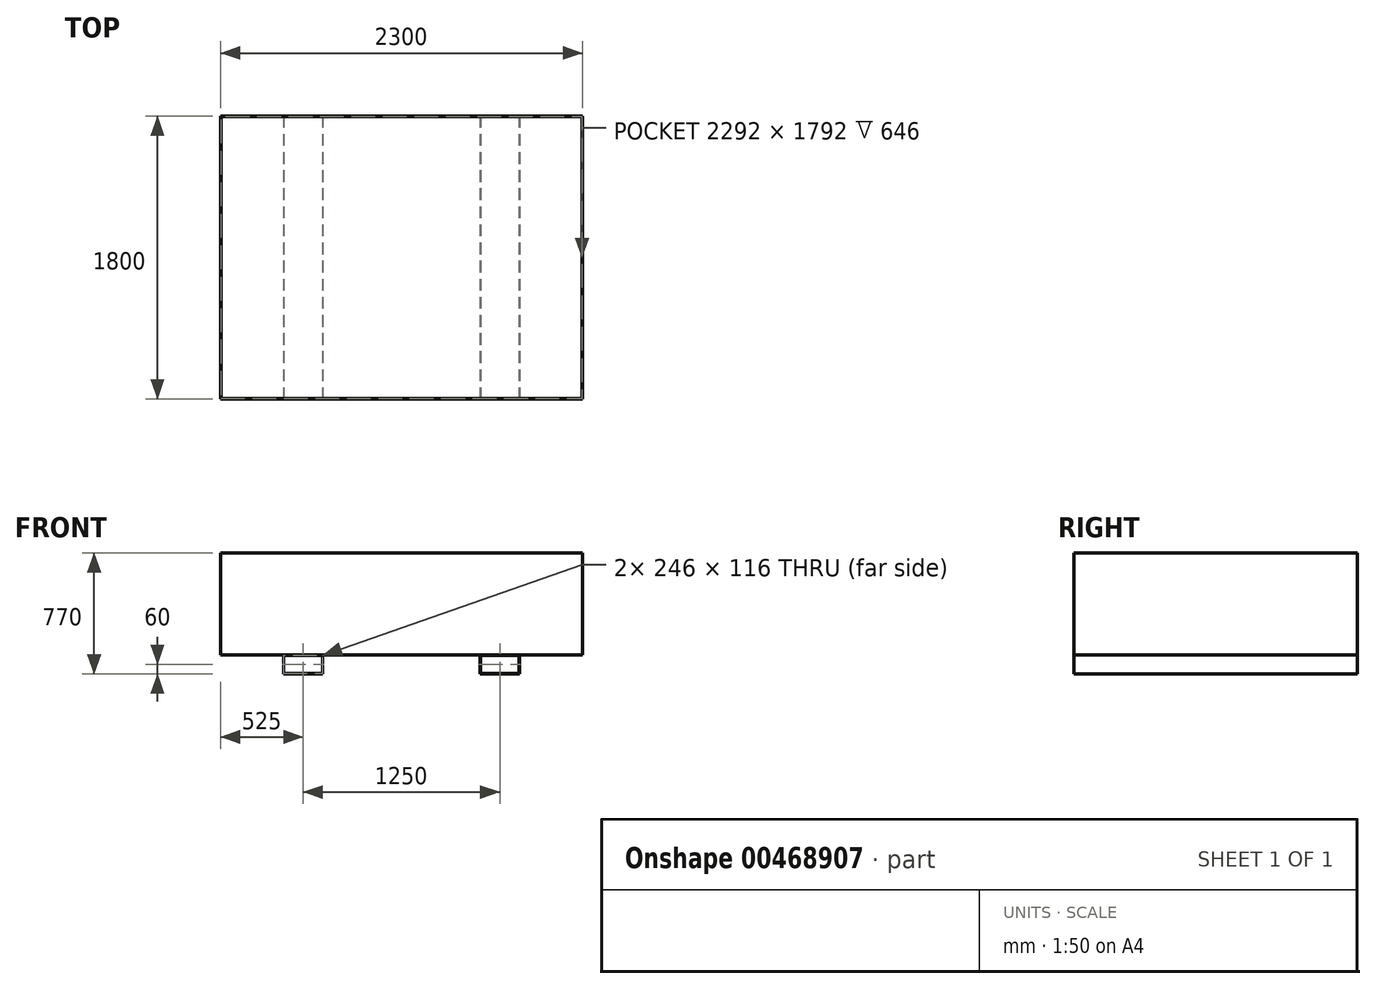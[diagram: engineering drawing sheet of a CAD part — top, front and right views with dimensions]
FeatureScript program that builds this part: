
annotation { "Feature Type Name" : "Feature", "Feature Type Description" : "" }
export const myFeature = defineFeature(function(context is Context, id is Id, definition is map)
    precondition{}
    {
        {
            var Q0;
            Q0=qCreatedBy(makeId("Top.planeOp"),FACE);
            var sketch = newSketch(context, id + "F0", { "sketchPlane" : qUnion([Q0])});
            skLineSegment(sketch, "E0.bottom", {"start": v(-1150, 1775.16) * mm, "end": v(1150, 1775.16) * mm});
            skLineSegment(sketch, "E0.top", {"start": v(-1150, -24.84) * mm, "end": v(1150, -24.84) * mm});
            skLineSegment(sketch, "E0.left", {"start": v(-1150, 1775.16) * mm, "end": v(-1150, -24.84) * mm});
            skLineSegment(sketch, "E0.right", {"start": v(1150, 1775.16) * mm, "end": v(1150, -24.84) * mm});
            skLineSegment(sketch, "E1", {"start": v(0, -153.05) * mm, "end": v(0, 1915.54) * mm, "construction": true});
            skSolve(sketch);
        }
        {
            var Q0;
            Q0=makeQuery(id+"F0.imprint","IMPRINT",FACE,{"disambiguationData":[TD([[makeQuery(id+"F0.imprint","IMPRINT",EDGE,{"derivedFrom":sQuery(id+"F0.wireOp",EDGE,"E0.bottom")}),-1.0]])]});
            extrude(context, id + "F1", {"entities" : qUnion([Q0]), "depth" : 650 * mm});
        }
        {
            var Q0;
            Q0=makeQuery(id+"F1.opExtrude","CAP_FACE",FACE,{"disambiguationData":[OSD([sQuery(id+"F0.wireOp",EDGE,"E0.bottom"),sQuery(id+"F0.wireOp",EDGE,"E0.top"),sQuery(id+"F0.wireOp",EDGE,"E0.left"),sQuery(id+"F0.wireOp",EDGE,"E0.right")])],"isStart":false});
            var Q1;
            Q1=makeQuery(id+"F1.opExtrude","SWEPT_BODY",BODY,{"disambiguationData":[OSD([sQuery(id+"F0.wireOp",EDGE,"E0.bottom"),sQuery(id+"F0.wireOp",EDGE,"E0.top"),sQuery(id+"F0.wireOp",EDGE,"E0.left"),sQuery(id+"F0.wireOp",EDGE,"E0.right")])]});
            shell(context, id + "F2", {"entities" : qUnion([Q0]), "parts" : qUnion([Q1]), "thickness" : 4 * mm});
        }
        {
            var Q0;
            Q0=makeQuery(id+"F1.opExtrude","SWEPT_FACE",FACE,{"disambiguationData":[OSD([sQuery(id+"F0.wireOp",EDGE,"E0.top")])]});
            var sketch = newSketch(context, id + "F3", { "sketchPlane" : qUnion([Q0])});
            skLineSegment(sketch, "E2.bottom", {"start": v(500, 0) * mm, "end": v(750, 0) * mm});
            skLineSegment(sketch, "E2.top", {"start": v(500, -120) * mm, "end": v(750, -120) * mm});
            skLineSegment(sketch, "E2.left", {"start": v(500, 0) * mm, "end": v(500, -120) * mm});
            skLineSegment(sketch, "E2.right", {"start": v(750, 0) * mm, "end": v(750, -120) * mm});
            skSolve(sketch);
        }
        {
            var Q0;
            Q0 = qSketchRegion(id + "F3", true);
            var Q1;
            Q1=makeQuery(id+"F1.opExtrude","SWEPT_FACE",FACE,{"disambiguationData":[OSD([sQuery(id+"F0.wireOp",EDGE,"E0.bottom")])]});
            extrude(context, id + "F4", {"entities" : qUnion([Q0]), "endBound" : BoundingType.UP_TO_SURFACE, "oppositeDirection" : true, "endBoundEntityFace" : qUnion([Q1]), "depth" : 25 * mm});
        }
        {
            var Q0;
            Q0=makeQuery(id+"F4.opExtrude","CAP_FACE",FACE,{"disambiguationData":[OSD([sQuery(id+"F3.wireOp",EDGE,"E2.bottom"),sQuery(id+"F3.wireOp",EDGE,"E2.top"),sQuery(id+"F3.wireOp",EDGE,"E2.left"),sQuery(id+"F3.wireOp",EDGE,"E2.right")])],"isStart":true});
            var Q1;
            Q1=makeQuery(id+"F4.opExtrude","CAP_FACE",FACE,{"disambiguationData":[OSD([sQuery(id+"F3.wireOp",EDGE,"E2.bottom"),sQuery(id+"F3.wireOp",EDGE,"E2.top"),sQuery(id+"F3.wireOp",EDGE,"E2.left"),sQuery(id+"F3.wireOp",EDGE,"E2.right")])],"isStart":false});
            shell(context, id + "F5", {"entities" : qUnion([Q0, Q1]), "thickness" : 2 * mm});
        }
        {
            var Q0;
            Q0=makeQuery(id+"F4.opExtrude","SWEPT_BODY",BODY,{"disambiguationData":[OSD([sQuery(id+"F3.wireOp",EDGE,"E2.bottom"),sQuery(id+"F3.wireOp",EDGE,"E2.top"),sQuery(id+"F3.wireOp",EDGE,"E2.left"),sQuery(id+"F3.wireOp",EDGE,"E2.right")])]});
            var Q1;
            Q1=qCreatedBy(makeId("Right.planeOp"),FACE);
            mirror(context, id + "F6", {"entities" : qUnion([Q0]), "mirrorPlane" : qUnion([Q1])});
        }
    });
